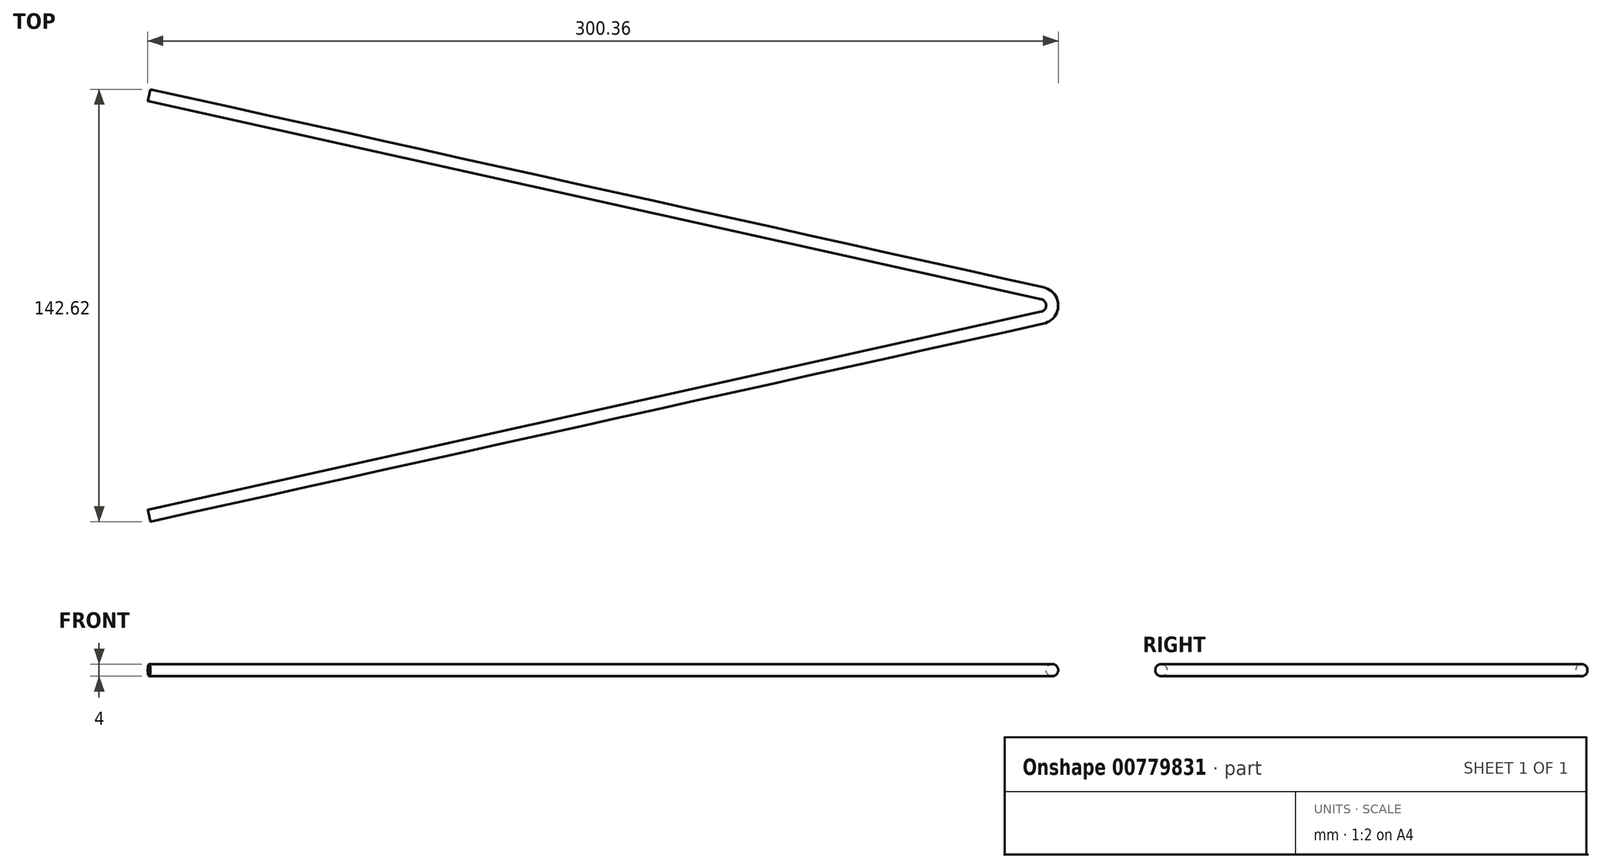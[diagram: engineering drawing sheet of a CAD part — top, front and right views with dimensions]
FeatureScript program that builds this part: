
annotation { "Feature Type Name" : "Feature", "Feature Type Description" : "" }
export const myFeature = defineFeature(function(context is Context, id is Id, definition is map)
    precondition{}
    {
        {
            var Q0;
            Q0=qCreatedBy(makeId("Top.planeOp"),FACE);
            var sketch = newSketch(context, id + "F0", { "sketchPlane" : qUnion([Q0])});
            skLineSegment(sketch, "E0", {"start": v(-312.86, 69.36) * mm, "end": v(312.86, -69.36) * mm, "construction": true});
            skLineSegment(sketch, "E1", {"start": v(312.86, 69.36) * mm, "end": v(-312.86, -69.36) * mm, "construction": true});
            skLineSegment(sketch, "E2", {"start": v(-312.86, 69.36) * mm, "end": v(-18.16, 4.03) * mm});
            skLineSegment(sketch, "E3", {"start": v(-312.86, -69.36) * mm, "end": v(-18.16, -4.03) * mm});
            skArc(sketch, "E4", {"start": v(-18.16, -4.03) * mm, "mid": v(-14.93, 0) * mm, "end": v(-18.16, 4.03) * mm});
            skSolve(sketch);
        }
        {
            var Q0;
            Q0=sQuery(id+"F0.wireOp",VERTEX,"E0.start");
            var Q1;
            Q1=sQuery(id+"F0.wireOp",EDGE,"E2");
            cPlane(context, id + "F1", {"entities" : qUnion([Q0, Q1]), "cplaneType" : CPlaneType.LINE_POINT, "offset" : 25 * mm, "width" : 150 * mm, "height" : 150 * mm});
        }
        {
            var Q0;
            Q0=qCreatedBy(id+"F1.planeOp",FACE);
            var sketch = newSketch(context, id + "F2", { "sketchPlane" : qUnion([Q0])});
            skCircle(sketch, "E5", {"center": v(0, 0) * mm, "radius": 2 * mm});
            skSolve(sketch);
        }
        {
            var Q0;
            Q0=makeQuery(id+"F2.imprint","IMPRINT",FACE,{"disambiguationData":[TD([[makeQuery(id+"F2.imprint","IMPRINT",EDGE,{"derivedFrom":sQuery(id+"F2.wireOp",EDGE,"E5")}),1.0]])]});
            var Q1;
            Q1=sQuery(id+"F0.wireOp",EDGE,"E2");
            var Q2;
            Q2=sQuery(id+"F0.wireOp",EDGE,"E4");
            var Q3;
            Q3=sQuery(id+"F0.wireOp",EDGE,"E3");
            sweep(context, id + "F3", {"profiles" : qUnion([Q0]), "path" : qUnion([Q1, Q2, Q3])});
        }
    });
